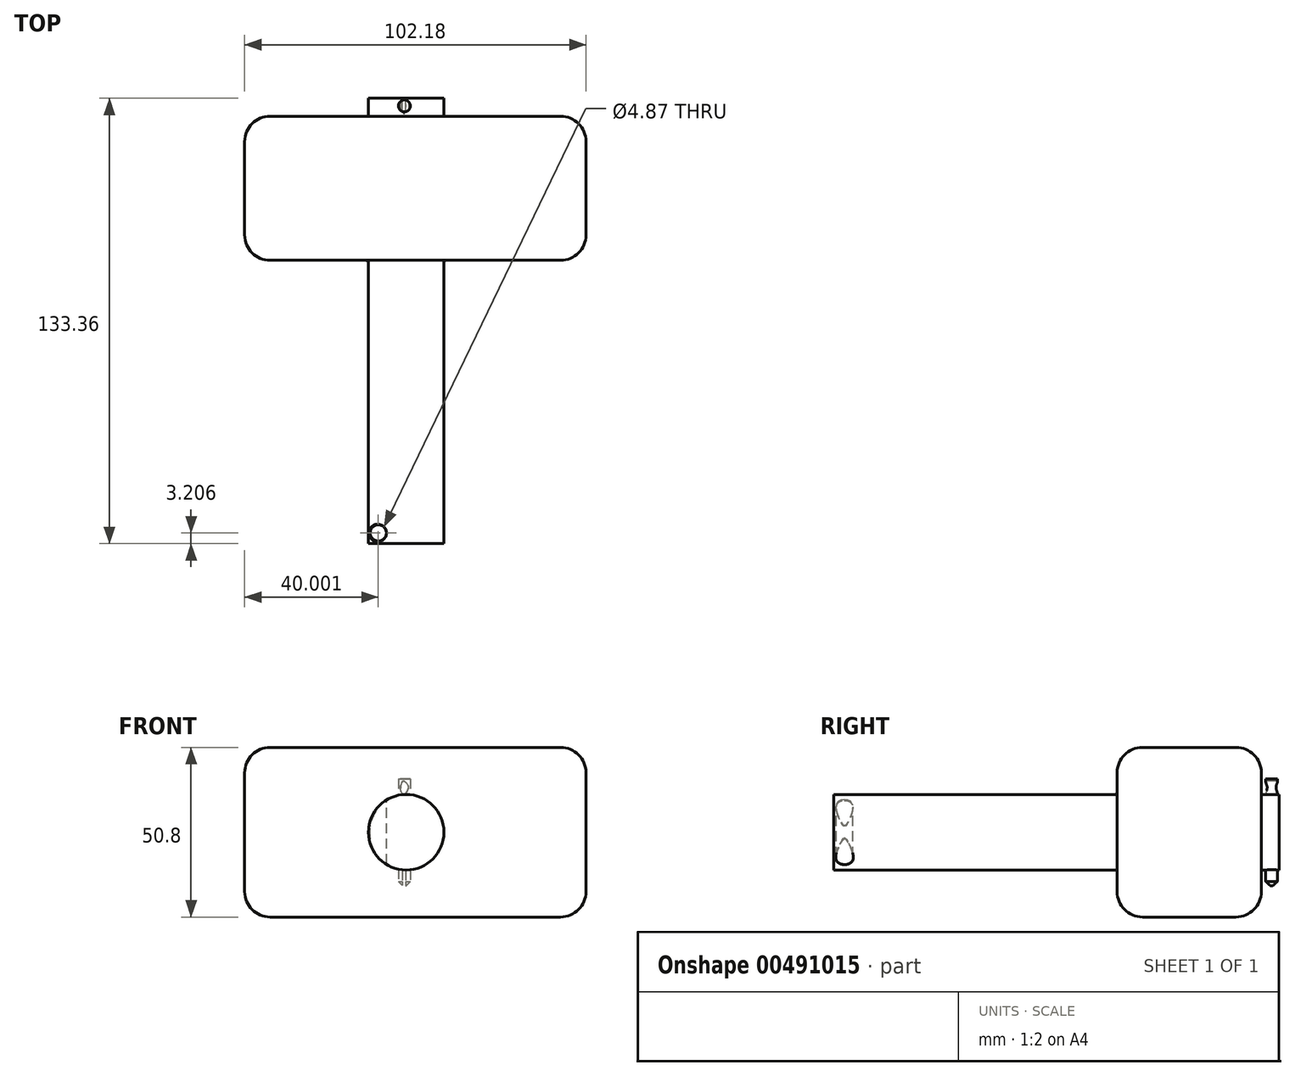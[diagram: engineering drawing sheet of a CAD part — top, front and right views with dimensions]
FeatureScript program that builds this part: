
annotation { "Feature Type Name" : "Feature", "Feature Type Description" : "" }
export const myFeature = defineFeature(function(context is Context, id is Id, definition is map)
    precondition{}
    {
        {
            var Q0;
            Q0=qCreatedBy(makeId("Top.planeOp"),FACE);
            var sketch = newSketch(context, id + "F0", { "sketchPlane" : qUnion([Q0])});
            skLineSegment(sketch, "E0.bottom", {"start": v(-54.4, 18.13) * mm, "end": v(47.78, 18.13) * mm});
            skLineSegment(sketch, "E0.top", {"start": v(-54.4, 61.3) * mm, "end": v(47.78, 61.3) * mm});
            skLineSegment(sketch, "E0.left", {"start": v(-54.4, 18.13) * mm, "end": v(-54.4, 61.3) * mm});
            skLineSegment(sketch, "E0.right", {"start": v(47.78, 18.13) * mm, "end": v(47.78, 61.3) * mm});
            skSolve(sketch);
        }
        {
            var Q0;
            Q0 = qSketchRegion(id + "F0", true);
            extrude(context, id + "F1", {"entities" : qUnion([Q0]), "endBound" : BoundingType.SYMMETRIC, "depth" : 50.8 * mm});
        }
        {
            var Q0;
            Q0=qCreatedBy(makeId("Front.planeOp"),FACE);
            var sketch = newSketch(context, id + "F2", { "sketchPlane" : qUnion([Q0])});
            skCircle(sketch, "E1", {"center": v(-6.04, 0) * mm, "radius": 11.3 * mm});
            skSolve(sketch);
        }
        {
            var Q0;
            Q0 = qSketchRegion(id + "F2", true);
            extrude(context, id + "F3", {"entities" : qUnion([Q0]), "operationType" : NewBodyOperationType.ADD, "endBound" : BoundingType.SYMMETRIC, "depth" : 133.35 * mm});
        }
        {
            var Q0;
            Q0=makeQuery(id+"F1.opExtrude","CAP_EDGE",EDGE,{"disambiguationData":[OSD([sQuery(id+"F0.wireOp",EDGE,"E0.left")])],"isStart":false});
            var Q1;
            Q1=makeQuery(id+"F1.opExtrude","CAP_EDGE",EDGE,{"disambiguationData":[OSD([sQuery(id+"F0.wireOp",EDGE,"E0.left")])],"isStart":true});
            var Q2;
            Q2=makeQuery(id+"F1.opExtrude","CAP_EDGE",EDGE,{"disambiguationData":[OSD([sQuery(id+"F0.wireOp",EDGE,"E0.right")])],"isStart":true});
            var Q3;
            Q3=makeQuery(id+"F1.opExtrude","CAP_EDGE",EDGE,{"disambiguationData":[OSD([sQuery(id+"F0.wireOp",EDGE,"E0.top")])],"isStart":true});
            var Q4;
            Q4=makeQuery(id+"F1.opExtrude","CAP_EDGE",EDGE,{"disambiguationData":[OSD([sQuery(id+"F0.wireOp",EDGE,"E0.bottom")])],"isStart":true});
            var Q5;
            Q5=makeQuery(id+"F1.opExtrude","SWEPT_EDGE",EDGE,{"disambiguationData":[OSD([sQuery(id+"F0.wireOp",EDGE,"E0.bottom"),sQuery(id+"F0.wireOp",EDGE,"E0.right")])]});
            var Q6;
            Q6=makeQuery(id+"F1.opExtrude","CAP_EDGE",EDGE,{"disambiguationData":[OSD([sQuery(id+"F0.wireOp",EDGE,"E0.right")])],"isStart":false});
            var Q7;
            Q7=makeQuery(id+"F1.opExtrude","CAP_EDGE",EDGE,{"disambiguationData":[OSD([sQuery(id+"F0.wireOp",EDGE,"E0.bottom")])],"isStart":false});
            var Q8;
            Q8=makeQuery(id+"F1.opExtrude","SWEPT_EDGE",EDGE,{"disambiguationData":[OSD([sQuery(id+"F0.wireOp",EDGE,"E0.top"),sQuery(id+"F0.wireOp",EDGE,"E0.left")])]});
            var Q9;
            Q9=makeQuery(id+"F1.opExtrude","SWEPT_EDGE",EDGE,{"disambiguationData":[OSD([sQuery(id+"F0.wireOp",EDGE,"E0.bottom"),sQuery(id+"F0.wireOp",EDGE,"E0.left")])]});
            var Q10;
            Q10=makeQuery(id+"F1.opExtrude","SWEPT_EDGE",EDGE,{"disambiguationData":[OSD([sQuery(id+"F0.wireOp",EDGE,"E0.top"),sQuery(id+"F0.wireOp",EDGE,"E0.right")])]});
            var Q11;
            Q11=makeQuery(id+"F1.opExtrude","CAP_EDGE",EDGE,{"disambiguationData":[OSD([sQuery(id+"F0.wireOp",EDGE,"E0.top")])],"isStart":false});
            fillet(context, id + "F4", {"entities" : qUnion([Q0, Q1, Q2, Q3, Q4, Q5, Q6, Q7, Q8, Q9, Q10, Q11]), "radius" : 7.62 * mm, "tangentPropagation" : true, "allowEdgeOverflow" : false});
        }
        {
            var Q0;
            Q0=qCreatedBy(makeId("Top.planeOp"),FACE);
            var sketch = newSketch(context, id + "F5", { "sketchPlane" : qUnion([Q0])});
            skCircle(sketch, "E2", {"center": v(-14.4, -63.47) * mm, "radius": 2.44 * mm});
            skSolve(sketch);
        }
        {
            var Q0;
            Q0 = qSketchRegion(id + "F5", true);
            extrude(context, id + "F6", {"entities" : qUnion([Q0]), "operationType" : NewBodyOperationType.REMOVE, "endBound" : BoundingType.SYMMETRIC, "oppositeDirection" : true, "depth" : 40.13 * mm});
        }
        {
            var Q0;
            Q0=qCreatedBy(makeId("Top.planeOp"),FACE);
            var sketch = newSketch(context, id + "F7", { "sketchPlane" : qUnion([Q0])});
            skCircle(sketch, "E3", {"center": v(-6.57, 64.38) * mm, "radius": 1.79 * mm});
            skSolve(sketch);
        }
        {
            var Q0;
            Q0 = qSketchRegion(id + "F7", true);
            extrude(context, id + "F8", {"entities" : qUnion([Q0]), "operationType" : NewBodyOperationType.ADD, "endBound" : BoundingType.SYMMETRIC, "depth" : 32 * mm});
        }
        {
            var Q0;
            Q0=qCreatedBy(makeId("Front.planeOp"),FACE);
            cPlane(context, id + "F9", {"entities" : qUnion([Q0]), "cplaneType" : CPlaneType.OFFSET, "offset" : 64.77 * mm, "oppositeDirection" : true, "width" : 152.4 * mm, "height" : 152.4 * mm});
        }
        {
            var Q0;
            Q0=qCreatedBy(id+"F9.planeOp",FACE);
            var sketch = newSketch(context, id + "F10", { "sketchPlane" : qUnion([Q0])});
            skFitSpline(sketch, "E4", {"points": [v(-7.03, 15.3) * mm, v(-7.7, 13.54) * mm, v(-7.5, 12.02) * mm, v(-7.03, 11.39) * mm, v(-6.44, 11.36) * mm, v(-5.4, 13.05) * mm, v(-5.53, 14.13) * mm, v(-6.04, 14.82) * mm, v(-7.03, 15.3) * mm]});
            skSolve(sketch);
        }
        {
            var Q0;
            Q0 = qSketchRegion(id + "F10", true);
            extrude(context, id + "F11", {"entities" : qUnion([Q0]), "operationType" : NewBodyOperationType.REMOVE, "endBound" : BoundingType.SYMMETRIC, "oppositeDirection" : true, "depth" : 4.93 * mm});
        }
        {
            var Q0;
            Q0=makeQuery(id+"F8.opExtrude","CAP_EDGE",EDGE,{"disambiguationData":[OSD([sQuery(id+"F7.wireOp",EDGE,"E3")])],"isStart":true});
            chamfer(context, id + "F12", {"entities" : qUnion([Q0]), "width" : 1.27 * mm, "tangentPropagation" : true});
        }
        {
            var Q0;
            Q0=makeQuery(id+"F3.boolean.opBoolean","INTERSECT",EDGE,{"derivedFrom":[makeQuery(id+"F1.opExtrude","SWEPT_FACE",FACE,{"disambiguationData":[OSD([sQuery(id+"F0.wireOp",EDGE,"E0.bottom")])]}),makeQuery(id+"F3.opExtrude","SWEPT_FACE",FACE,{"disambiguationData":[OSD([sQuery(id+"F2.wireOp",EDGE,"E1")])]})]});
            fillet(context, id + "F13", {"entities" : qUnion([Q0]), "radius" : 0.64 * mm, "tangentPropagation" : true, "allowEdgeOverflow" : false});
        }
        {
            var Q0;
            {var subQ0=sQuery(id+"F2.wireOp",EDGE,"E1");Q0=makeQuery(id+"F6.boolean.opBoolean","INTERSECT",EDGE,{"disambiguationData":[OD(0.0)],"derivedFrom":[makeQuery(id+"F3.boolean.opBoolean","SPLIT",FACE,{"disambiguationData":[TD([makeQuery(id+"F1.opExtrude","SWEPT_FACE",FACE,{"disambiguationData":[OSD([sQuery(id+"F0.wireOp",EDGE,"E0.bottom")])]})])],"derivedFrom":makeQuery(id+"F3.opExtrude","SWEPT_FACE",FACE,{"disambiguationData":[OSD([subQ0])]})}),makeQuery(id+"F6.opExtrude","SWEPT_FACE",FACE,{"disambiguationData":[OSD([sQuery(id+"F5.wireOp",EDGE,"E2")])]})]});}
            var Q1;
            {var subQ0=sQuery(id+"F2.wireOp",EDGE,"E1");Q1=makeQuery(id+"F6.boolean.opBoolean","INTERSECT",EDGE,{"disambiguationData":[OD(1.0)],"derivedFrom":[makeQuery(id+"F3.boolean.opBoolean","SPLIT",FACE,{"disambiguationData":[TD([makeQuery(id+"F1.opExtrude","SWEPT_FACE",FACE,{"disambiguationData":[OSD([sQuery(id+"F0.wireOp",EDGE,"E0.bottom")])]})])],"derivedFrom":makeQuery(id+"F3.opExtrude","SWEPT_FACE",FACE,{"disambiguationData":[OSD([subQ0])]})}),makeQuery(id+"F6.opExtrude","SWEPT_FACE",FACE,{"disambiguationData":[OSD([sQuery(id+"F5.wireOp",EDGE,"E2")])]})]});}
            fillet(context, id + "F14", {"entities" : qUnion([Q0, Q1]), "radius" : 0.2 * mm, "tangentPropagation" : true, "allowEdgeOverflow" : false});
        }
        {
            var Q0;
            Q0=qCreatedBy(id+"F9.planeOp",FACE);
            var sketch = newSketch(context, id + "F15", { "sketchPlane" : qUnion([Q0])});
            skLineSegment(sketch, "E5.bottom", {"start": v(-6.2, -16.1) * mm, "end": v(-7.18, -16.1) * mm});
            skLineSegment(sketch, "E5.top", {"start": v(-6.2, -11.39) * mm, "end": v(-7.18, -11.39) * mm});
            skLineSegment(sketch, "E5.left", {"start": v(-6.2, -16.1) * mm, "end": v(-6.2, -11.39) * mm});
            skLineSegment(sketch, "E5.right", {"start": v(-7.18, -16.1) * mm, "end": v(-7.18, -11.39) * mm});
            skSolve(sketch);
        }
        {
            var Q0;
            Q0 = qSketchRegion(id + "F15", true);
            extrude(context, id + "F16", {"entities" : qUnion([Q0]), "operationType" : NewBodyOperationType.REMOVE, "endBound" : BoundingType.SYMMETRIC, "depth" : 4.78 * mm});
        }
    });
